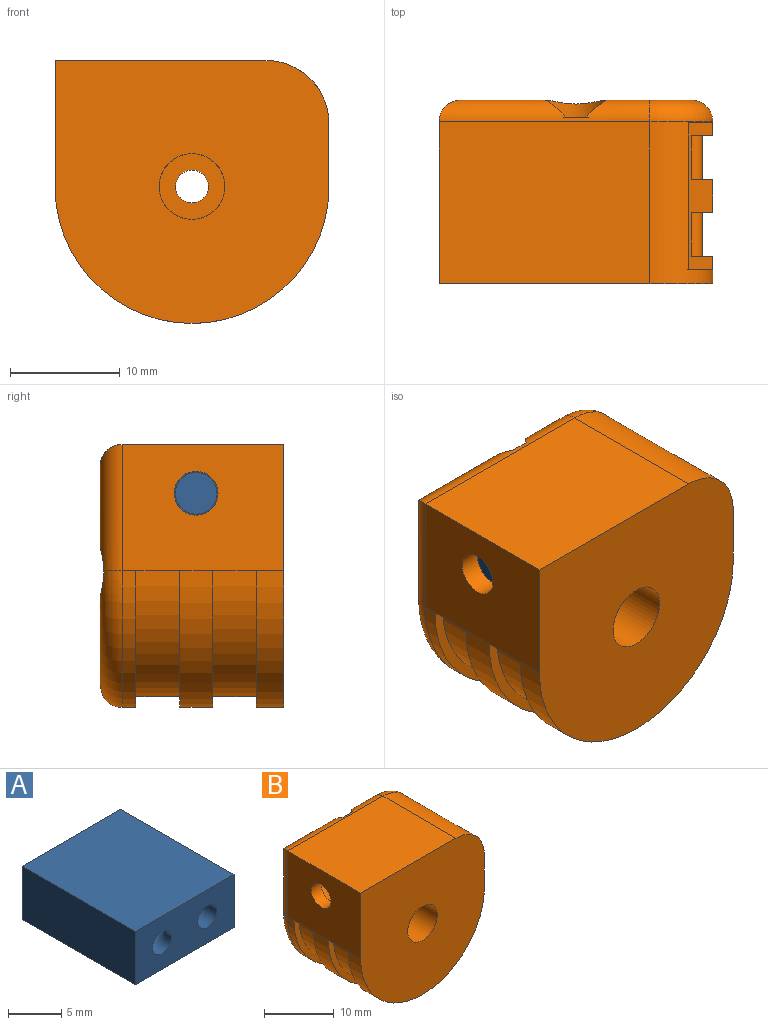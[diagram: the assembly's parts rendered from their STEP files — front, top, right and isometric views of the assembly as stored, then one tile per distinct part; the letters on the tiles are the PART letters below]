
ASSEMBLY  parts=2 mates=1
PART A: 9 faces, bbox 13.1x15x6.1 mm
  f0: plane 15x13.1mm, normal (0,0,-1), area 196.5mm2, adj f1,f3,f4,f7
  f1: plane 15x6.1mm, normal (1,0,0), area 91.5mm2, adj f0,f2,f4,f7
  f2: plane 15x13.1mm, normal (0,0,1), area 196.5mm2, adj f1,f3,f4,f7
  f3: plane 15x6.1mm, normal (-1,0,0), area 91.5mm2, adj f0,f2,f4,f7
  f4: plane 13.1x6.1mm, normal (0,1,0), area 68.6mm2, adj f0,f1,f2,f3,f5
  f5: cylinder r=1.9mm len=9mm, axis (0,1,0), area 107.4mm2, adj f4,f6
  f6: plane 3.8x3.8mm, normal (0,1,0), area 11.3mm2, adj f5
  f7: plane 13.1x6.1mm, normal (0,-1,0), area 70.1mm2, adj f0,f1,f2,f3,f8
  f8: torus R=3mm, axis (0,0,-1), area 74mm2, adj f7
PART B: 62 faces, bbox 27.1x16.8x25.5 mm
  f0: plane 7.57x7.13mm, normal (0,1,0), area 47.9mm2, adj f34,f48,f49,f50,f51,f60,f61
  f1: plane 7.57x7.13mm, normal (0,1,0), area 44.9mm2, adj f35,f37,f38,f39,f40,f57,f59,f61
  f2: plane 7.56x7.56mm, normal (0,1,0), area 32.5mm2, adj f40,f41,f42,f43,f44,f58
  f3: cylinder r=3mm len=13.55mm, axis (0,1,0), area 255.4mm2, adj f14,f53
  f4: plane 19.25x14.75mm, normal (0,0,1), area 283.9mm2, adj f11,f13,f14,f61
  f5: cylinder r=3.6mm len=7.2mm, axis (0,1,0), area 13.6mm2, adj f33,f36
  f6: plane 3.8x3mm, normal (1,0,0), area 11.4mm2, adj f7,f15,f20,f27
  f7: cylinder r=12.5mm len=25mm, axis (0,1,0), area 117.8mm2, adj f6,f13,f20,f27
  f8: plane 3.8x1.25mm, normal (1,0,0), area 4.8mm2, adj f9,f15,f21,f57
  f9: cylinder r=12.5mm len=25mm, axis (0,1,0), area 49.1mm2, adj f8,f13,f21,f58
  f10: plane 5.75x2.5mm, normal (1,0,0), area 11.9mm2, adj f11,f12,f14,f15,f17,f26
  f11: cylinder r=5.75mm len=14.75mm, axis (0,1,0), area 62.4mm2, adj f4,f10,f14,f17,f18,f59
  f12: cylinder r=12.5mm len=25mm, axis (0,1,0), area 98.2mm2, adj f10,f13,f14,f26
  f13: plane 14.75x11.5mm, normal (-1,0,0), area 157.1mm2, adj f4,f7,f9,f12,f14,f24,f29,f56
  f14: plane 25x24mm, normal (0,-1,0), area 497.6mm2, adj f3,f4,f10,f11,f12,f13
  f15: plane 23x13.5mm, normal (0,0,1), area 294.5mm2, adj f6,f8,f10,f16,f17,f19,f20,f21
  f16: plane 23x6.5mm, normal (0,-1,0), area 146.4mm2, adj f15,f18,f19,f57,f59
  f17: plane 23x6.5mm, normal (0,1,0), area 146.4mm2, adj f10,f11,f15,f18,f19
  f18: plane 20.77x13.5mm, normal (0,0,-1), area 280.3mm2, adj f11,f16,f17,f19
  f19: plane 13.5x6.5mm, normal (1,0,0), area 75.2mm2, adj f15,f16,f17,f18,f56
  f20: plane 25x16.3mm, normal (0,1,0), area 41.7mm2, adj f6,f7,f15,f22,f23,f24,f32
  f21: plane 25x16.3mm, normal (0,-1,0), area 41.7mm2, adj f8,f9,f15,f22,f23,f24,f32
  f22: plane 4x2.8mm, normal (1,0,0), area 11.2mm2, adj f20,f21,f23,f32
  f23: cylinder r=11.5mm len=23mm, axis (0,1,0), area 144.5mm2, adj f20,f21,f22,f24
  f24: plane 4x1mm, normal (0,0,-1), area 4mm2, adj f13,f20,f21,f23
  f25: plane 4x2.8mm, normal (1,0,0), area 11.2mm2, adj f26,f27,f28,f31
  f26: plane 25x16.3mm, normal (0,1,0), area 41.7mm2, adj f10,f12,f15,f25,f28,f29,f31
  f27: plane 25x16.3mm, normal (0,-1,0), area 41.7mm2, adj f6,f7,f15,f25,f28,f29,f31
  f28: cylinder r=11.5mm len=23mm, axis (0,1,0), area 144.5mm2, adj f25,f26,f27,f29
  f29: plane 4x1mm, normal (0,0,-1), area 4mm2, adj f13,f26,f27,f28
  f30: plane 7.56x7.56mm, normal (0,1,0), area 32.5mm2, adj f44,f45,f46,f47,f48,f58
  f31: cylinder r=1mm len=4mm, axis (0,1,0), area 6.3mm2, adj f15,f25,f26,f27
  f32: cylinder r=1mm len=4mm, axis (0,1,0), area 6.3mm2, adj f15,f20,f21,f22
  f33: plane 7.2x7.2mm, normal (0,1,0), area 14.3mm2, adj f5,f54
  f34: cylinder r=3.1mm len=2.96mm, axis (0,1,0), area 4.7mm2, adj f0,f36,f51,f61
  f35: cylinder r=3.1mm len=2.96mm, axis (0,1,0), area 4.7mm2, adj f1,f36,f37,f61
  f36: plane 23.2x23.06mm, normal (0,1,0), area 191.9mm2, adj f5,f34,f35,f37,f38,f39,f40,f41
  f37: plane 5.38x1.6mm, normal (-1,0,0), area 8.6mm2, adj f1,f35,f36,f38
  f38: plane 1.6x0.02mm, normal (-0.71,0,-0.71), area 0.1mm2, adj f1,f36,f37,f39
  f39: plane 5.38x1.6mm, normal (0,0,-1), area 8.6mm2, adj f1,f36,f38,f40
  f40: cylinder r=3.1mm len=6.2mm, axis (0,1,0), area 14.6mm2, adj f1,f2,f36,f39,f41,f57,f58
  f41: plane 5.38x1.6mm, normal (0,0,1), area 8.6mm2, adj f2,f36,f40,f42
  f42: plane 1.6x0.02mm, normal (-0.71,0,0.71), area 0.1mm2, adj f2,f36,f41,f43
  f43: plane 5.38x1.6mm, normal (-1,0,0), area 8.6mm2, adj f2,f36,f42,f44
  f44: cylinder r=3.1mm len=6.2mm, axis (0,1,0), area 14.5mm2, adj f2,f30,f36,f43,f45,f58
  f45: plane 5.38x1.6mm, normal (1,0,0), area 8.6mm2, adj f30,f36,f44,f46
  f46: plane 1.6x0.02mm, normal (0.71,0,0.71), area 0mm2, adj f30,f36,f45,f47
  f47: plane 5.38x1.6mm, normal (0,0,1), area 8.6mm2, adj f30,f36,f46,f48
  f48: cylinder r=3.1mm len=6.2mm, axis (0,1,0), area 14.6mm2, adj f0,f30,f36,f47,f49,f58,f60
  f49: plane 5.38x1.6mm, normal (0,0,-1), area 8.6mm2, adj f0,f36,f48,f50
  f50: cylinder r=4.5mm len=1.6mm, axis (0,1,0), area 0mm2, adj f0,f36,f49,f51
  f51: plane 5.38x1.6mm, normal (1,0,0), area 8.6mm2, adj f0,f34,f36,f50
  f52: cylinder r=1.5mm len=3mm, axis (0,1,0), area 14.1mm2, adj f53,f55
  f53: plane 6x6mm, normal (0,-1,0), area 21.2mm2, adj f3,f52
  f54: cylinder r=2.9mm len=5.8mm, axis (0,-1,0), area 9.1mm2, adj f33,f55
  f55: plane 5.8x5.8mm, normal (0,1,0), area 19.4mm2, adj f52,f54
  f56: cylinder r=2mm len=4mm, axis (-1,0,0), area 25.1mm2, adj f13,f19
  f57: cylinder r=2mm len=5.75mm, axis (0,0,1), area 16.2mm2, adj f1,f8,f16,f40,f58,f59
  f58: torus R=10.5mm, axis (0,-1,0), area 107.6mm2, adj f2,f9,f30,f40,f44,f48,f57,f60
  f59: torus R=3.75mm, axis (0,-1,0), area 24.8mm2, adj f1,f11,f16,f57,f61
  f60: cylinder r=2mm len=11.5mm, axis (0,0,-1), area 32mm2, adj f0,f13,f48,f58,f61
  f61: cylinder r=2mm len=19.25mm, axis (-1,0,0), area 47mm2, adj f0,f1,f4,f34,f35,f36,f59,f60
PLACE A rot(axis=(0,0,1),90deg) t=(-7.97,-1.46,5.5)mm
PLACE B t=(1.43,7.29,-1.55)mm
MATE slider A.f5 <-> B.f56  axis (-1,0,0) through (-7.97,-1.46,5.5)mm
